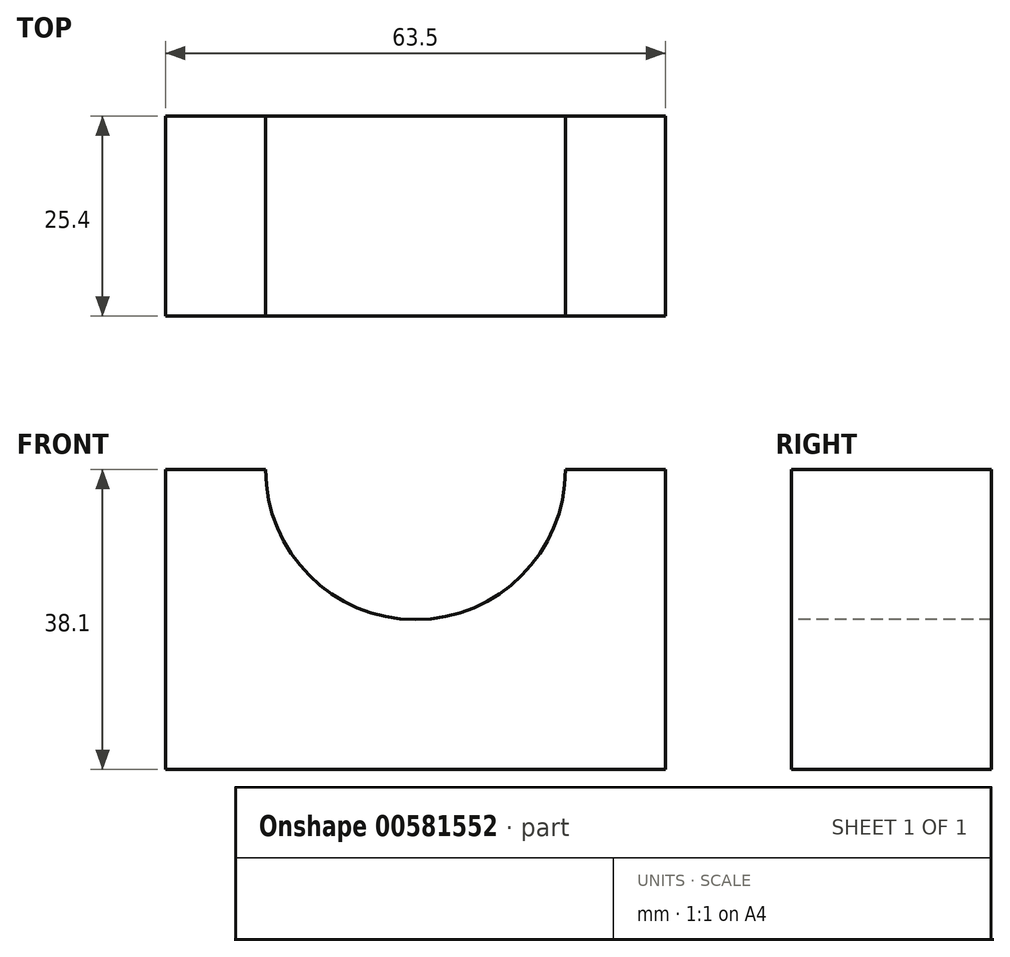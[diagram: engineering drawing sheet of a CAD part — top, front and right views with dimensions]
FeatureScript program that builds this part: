
annotation { "Feature Type Name" : "Feature", "Feature Type Description" : "" }
export const myFeature = defineFeature(function(context is Context, id is Id, definition is map)
    precondition{}
    {
        {
            var Q0;
            Q0=qCreatedBy(makeId("Front.planeOp"),FACE);
            var sketch = newSketch(context, id + "F0", { "sketchPlane" : qUnion([Q0])});
            skLineSegment(sketch, "E0", {"start": v(-66.92, 55.93) * mm, "end": v(-66.92, 17.83) * mm});
            skLineSegment(sketch, "E1", {"start": v(-66.92, 17.83) * mm, "end": v(-3.42, 17.83) * mm});
            skLineSegment(sketch, "E2", {"start": v(-3.42, 17.83) * mm, "end": v(-3.42, 55.93) * mm});
            skLineSegment(sketch, "E3", {"start": v(-3.42, 55.93) * mm, "end": v(-66.92, 55.93) * mm});
            skSolve(sketch);
        }
        {
            var Q0;
            Q0 = qSketchRegion(id + "F0", true);
            extrude(context, id + "F1", {"entities" : qUnion([Q0]), "depth" : 25.4 * mm, "offsetDistance" : 25.4 * mm});
        }
        {
            var Q0;
            Q0=makeQuery(id+"F1.opExtrude","CAP_FACE",FACE,{"disambiguationData":[OSD([sQuery(id+"F0.wireOp",EDGE,"E0"),sQuery(id+"F0.wireOp",EDGE,"E1"),sQuery(id+"F0.wireOp",EDGE,"E2"),sQuery(id+"F0.wireOp",EDGE,"E3")])],"isStart":false});
            var sketch = newSketch(context, id + "F2", { "sketchPlane" : qUnion([Q0])});
            skCircle(sketch, "E4", {"center": v(-35.17, 55.93) * mm, "radius": 19.05 * mm});
            skSolve(sketch);
        }
        {
            var Q0;
            Q0 = qSketchRegion(id + "F2", true);
            extrude(context, id + "F3", {"entities" : qUnion([Q0]), "operationType" : NewBodyOperationType.REMOVE, "oppositeDirection" : true, "depth" : 25.4 * mm, "offsetDistance" : 25.4 * mm});
        }
    });
